# Revit family: РОСМА_КлапанЭлектромагнитный_СК-ВТ
name_source: partatom
category: Арматура трубопроводов
revit_build: Autodesk Revit 2018 (Build: 20180423_1000(x64)
units: mm (PartAtom-declared; Revit-internal decimal feet)

## family parameters
Всегда вертикально = Да
На основе рабочей плоскости = Нет
Общий = Нет
При загрузке вырезать с полостями = Да
Размер круглого соединителя = Использовать диаметр
Тип детали = Вставляется

## types (1)
- СК-ВТ
    ADSK_Единица измерения = шт.
    ADSK_Количество = 1
    Table1 = размеры_сквт
    Table2 = спец_сквт
    URL = https://rosma.spb.ru
    Изготовитель = ЗАО "РОСМА"
    Климатическое исполнение = Группа В3 по ГОСТ Р 52931; климатическое исполнение УХЛ категории 3.1 по ГОСТ 15150
    Материал корпуса 1 = _Нержавеющая сталь
    Материал корпуса 2 = _Черный пластик
    Материал корпуса 3 = _Стекло
    Минимальное раб. давление,МПа = 0,05
    Надежность = 500000
    Номинальное напряжение = ~220 В, -24В
    Описание = Тип СК-ВТ. Клапаны двухпозиционные двухходовые электромагнитные предназначены для автоматического управления (открытие, закрытие) потоками воды, масла, сжатого воздуха, пара, газов и прочих агрессивных сред повышенной температуры. Непрямого действия.
    Степень защиты катушки = IP65, DIN-разъем
    Температура окр. среды = от -10°С до +80°С
    Температура раб. среды = от -20°С до +120°С
    Техническая документация = ТУ 3712-001-4719015564-2015
